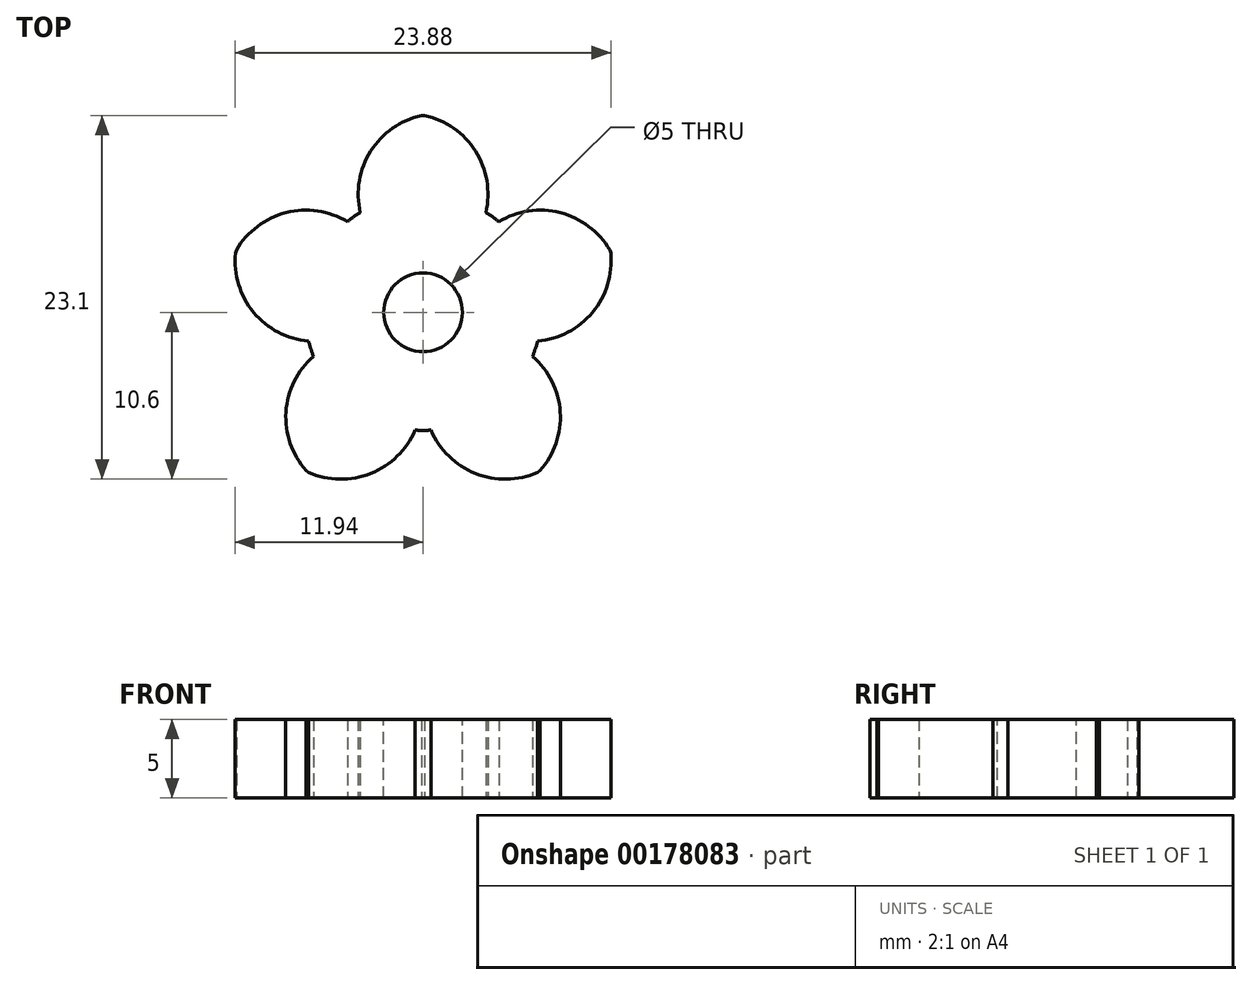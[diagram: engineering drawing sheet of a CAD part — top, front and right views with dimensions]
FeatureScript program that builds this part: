
annotation { "Feature Type Name" : "Feature", "Feature Type Description" : "" }
export const myFeature = defineFeature(function(context is Context, id is Id, definition is map)
    precondition{}
    {
        {
            var Q0;
            Q0=qCreatedBy(makeId("Top.planeOp"),FACE);
            var sketch = newSketch(context, id + "F0", { "sketchPlane" : qUnion([Q0])});
            skCircle(sketch, "E0", {"center": v(0, 0) * mm, "radius": 7.5 * mm});
            skLineSegment(sketch, "E1", {"start": v(0, 0) * mm, "end": v(0, 7.5) * mm, "construction": true});
            skLineSegment(sketch, "E2", {"start": v(0, 12.5) * mm, "end": v(-0.1, 12.5) * mm});
            skArc(sketch, "E3", {"start": v(-0.1, 12.5) * mm, "mid": v(-3.33, 10.24) * mm, "end": v(-3.99, 6.35) * mm});
            skArc(sketch, "E4.MirrorCS", {"start": v(0.1, 12.5) * mm, "mid": v(3.33, 10.24) * mm, "end": v(3.99, 6.35) * mm});
            skLineSegment(sketch, "E5.MirrorCS", {"start": v(0, 12.5) * mm, "end": v(0.1, 12.5) * mm});
            skArc(sketch, "E6.1.0", {"start": v(-11.92, 3.77) * mm, "mid": v(-10.76, 0) * mm, "end": v(-7.27, -1.83) * mm});
            skLineSegment(sketch, "E6.1.1", {"start": v(-11.89, 3.86) * mm, "end": v(-11.92, 3.77) * mm});
            skLineSegment(sketch, "E6.1.2", {"start": v(-11.89, 3.86) * mm, "end": v(-11.86, 3.96) * mm});
            skArc(sketch, "E6.1.3", {"start": v(-11.86, 3.96) * mm, "mid": v(-8.7, 6.33) * mm, "end": v(-4.8, 5.76) * mm});
            skArc(sketch, "E6.2.0", {"start": v(-7.27, -10.17) * mm, "mid": v(-3.33, -10.24) * mm, "end": v(-0.5, -7.48) * mm});
            skLineSegment(sketch, "E6.2.1", {"start": v(-7.35, -10.11) * mm, "end": v(-7.27, -10.17) * mm});
            skLineSegment(sketch, "E6.2.2", {"start": v(-7.35, -10.11) * mm, "end": v(-7.43, -10.05) * mm});
            skArc(sketch, "E6.2.3", {"start": v(-7.43, -10.05) * mm, "mid": v(-8.7, -6.33) * mm, "end": v(-6.96, -2.8) * mm});
            skArc(sketch, "E6.3.0", {"start": v(7.43, -10.05) * mm, "mid": v(8.7, -6.33) * mm, "end": v(6.96, -2.8) * mm});
            skLineSegment(sketch, "E6.3.1", {"start": v(7.35, -10.11) * mm, "end": v(7.43, -10.05) * mm});
            skLineSegment(sketch, "E6.3.2", {"start": v(7.35, -10.11) * mm, "end": v(7.27, -10.17) * mm});
            skArc(sketch, "E6.3.3", {"start": v(7.27, -10.17) * mm, "mid": v(3.33, -10.24) * mm, "end": v(0.5, -7.48) * mm});
            skArc(sketch, "E6.4.0", {"start": v(11.86, 3.96) * mm, "mid": v(8.7, 6.33) * mm, "end": v(4.8, 5.76) * mm});
            skLineSegment(sketch, "E6.4.1", {"start": v(11.89, 3.86) * mm, "end": v(11.86, 3.96) * mm});
            skLineSegment(sketch, "E6.4.2", {"start": v(11.89, 3.86) * mm, "end": v(11.92, 3.77) * mm});
            skArc(sketch, "E6.4.3", {"start": v(11.92, 3.77) * mm, "mid": v(10.76, 0) * mm, "end": v(7.27, -1.83) * mm});
            skSolve(sketch);
        }
        {
            var Q0;
            Q0=qSketchRegion(id+"F0",true);
            extrude(context, id + "F1", {"entities" : qUnion([Q0]), "depth" : 5 * mm});
        }
        {
            var Q0;
            Q0=makeQuery(id+"F1.opExtrude","CAP_FACE",FACE,{"disambiguationData":[OSD([sQuery(id+"F0.wireOp",EDGE,"E0"),sQuery(id+"F0.wireOp",EDGE,"E2"),sQuery(id+"F0.wireOp",EDGE,"E3"),sQuery(id+"F0.wireOp",EDGE,"E4.MirrorCS"),sQuery(id+"F0.wireOp",EDGE,"E5.MirrorCS"),sQuery(id+"F0.wireOp",EDGE,"E6.1.0"),sQuery(id+"F0.wireOp",EDGE,"E6.1.1"),sQuery(id+"F0.wireOp",EDGE,"E6.1.2"),sQuery(id+"F0.wireOp",EDGE,"E6.1.3"),sQuery(id+"F0.wireOp",EDGE,"E6.2.0"),sQuery(id+"F0.wireOp",EDGE,"E6.2.1"),sQuery(id+"F0.wireOp",EDGE,"E6.2.2"),sQuery(id+"F0.wireOp",EDGE,"E6.2.3"),sQuery(id+"F0.wireOp",EDGE,"E6.3.0"),sQuery(id+"F0.wireOp",EDGE,"E6.3.1"),sQuery(id+"F0.wireOp",EDGE,"E6.3.2"),sQuery(id+"F0.wireOp",EDGE,"E6.3.3"),sQuery(id+"F0.wireOp",EDGE,"E6.4.0"),sQuery(id+"F0.wireOp",EDGE,"E6.4.1"),sQuery(id+"F0.wireOp",EDGE,"E6.4.2"),sQuery(id+"F0.wireOp",EDGE,"E6.4.3")])],"isStart":false});
            var sketch = newSketch(context, id + "F2", { "sketchPlane" : qUnion([Q0])});
            skCircle(sketch, "E7", {"center": v(0, 0) * mm, "radius": 2.5 * mm});
            skSolve(sketch);
        }
        {
            var Q0;
            Q0=qSketchRegion(id+"F2",true);
            extrude(context, id + "F3", {"entities" : qUnion([Q0]), "operationType" : NewBodyOperationType.REMOVE, "endBound" : BoundingType.THROUGH_ALL, "oppositeDirection" : true, "depth" : 5 * mm});
        }
    });
